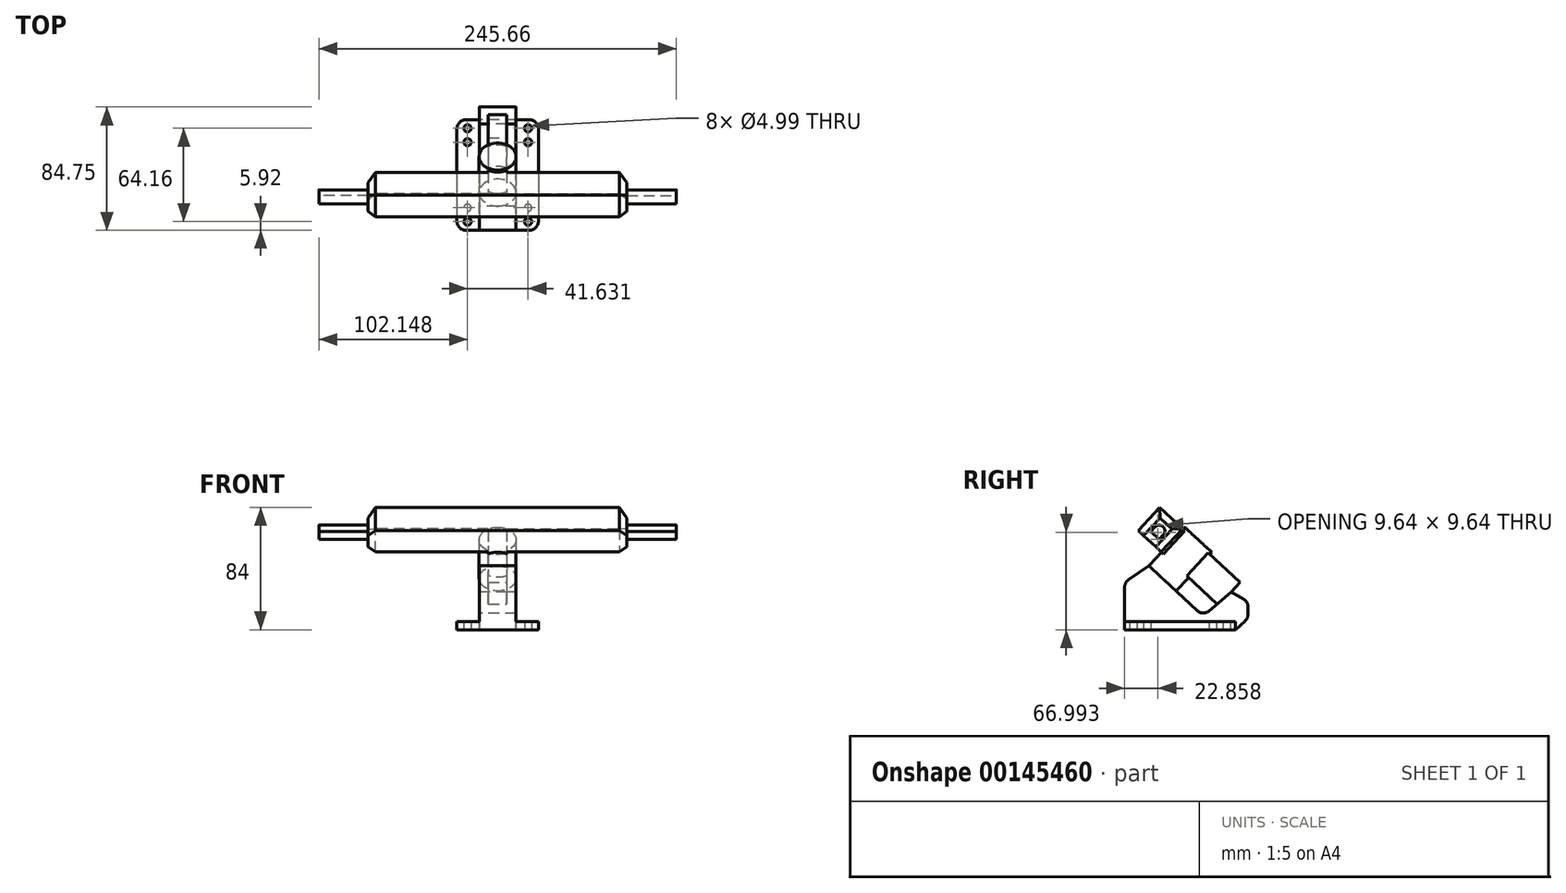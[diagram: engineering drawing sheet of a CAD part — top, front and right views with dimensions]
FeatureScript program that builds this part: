
annotation { "Feature Type Name" : "Feature", "Feature Type Description" : "" }
export const myFeature = defineFeature(function(context is Context, id is Id, definition is map)
    precondition{}
    {
        {
            var Q0;
            Q0=qCreatedBy(makeId("Top.planeOp"),FACE);
            var sketch = newSketch(context, id + "F0", { "sketchPlane" : qUnion([Q0])});
            skLineSegment(sketch, "E0.bottom", {"start": v(-21.65, 38) * mm, "end": v(21.65, 38) * mm});
            skLineSegment(sketch, "E0.top", {"start": v(-21.65, -38) * mm, "end": v(21.65, -38) * mm});
            skLineSegment(sketch, "E0.left", {"start": v(-28, 31.65) * mm, "end": v(-28, -31.65) * mm});
            skLineSegment(sketch, "E0.right", {"start": v(28, 31.65) * mm, "end": v(28, -31.65) * mm});
            skPoint(sketch, "E0.middle", {"position": v(0, 0) * mm});
            skLineSegment(sketch, "E1", {"start": v(20.95, 38) * mm, "end": v(20.95, -38) * mm, "construction": true});
            skLineSegment(sketch, "E2", {"start": v(-20.68, 38) * mm, "end": v(-20.68, -38) * mm, "construction": true});
            skLineSegment(sketch, "E3", {"start": v(-28, 32.08) * mm, "end": v(28, 32.08) * mm, "construction": true});
            skLineSegment(sketch, "E4", {"start": v(-28, 22.52) * mm, "end": v(28, 22.52) * mm, "construction": true});
            skLineSegment(sketch, "E5", {"start": v(-28, -22.52) * mm, "end": v(28, -22.52) * mm, "construction": true});
            skLineSegment(sketch, "E6", {"start": v(28, -32.08) * mm, "end": v(-28, -32.08) * mm, "construction": true});
            skCircle(sketch, "E7", {"center": v(-20.68, -32.08) * mm, "radius": 2.5 * mm});
            skCircle(sketch, "E8", {"center": v(-20.68, -22.52) * mm, "radius": 2.5 * mm});
            skCircle(sketch, "E9", {"center": v(-20.68, 22.52) * mm, "radius": 2.5 * mm});
            skCircle(sketch, "E10", {"center": v(-20.68, 32.08) * mm, "radius": 2.5 * mm});
            skCircle(sketch, "E11", {"center": v(20.95, 32.08) * mm, "radius": 2.5 * mm});
            skCircle(sketch, "E12", {"center": v(20.95, 22.52) * mm, "radius": 2.5 * mm});
            skCircle(sketch, "E13", {"center": v(20.95, -22.52) * mm, "radius": 2.5 * mm});
            skCircle(sketch, "E14", {"center": v(20.95, -32.08) * mm, "radius": 2.5 * mm});
            skPoint(sketch, "E15.visualSharp", {"position": v(-28, 38) * mm});
            skArc(sketch, "E15.filletArc", {"start": v(-21.65, 38) * mm, "mid": v(-26.14, 36.14) * mm, "end": v(-28, 31.65) * mm});
            skPoint(sketch, "E16.visualSharp", {"position": v(-28, -38) * mm});
            skArc(sketch, "E16.filletArc", {"start": v(-28, -31.65) * mm, "mid": v(-26.14, -36.14) * mm, "end": v(-21.65, -38) * mm});
            skPoint(sketch, "E17.visualSharp", {"position": v(28, -38) * mm});
            skArc(sketch, "E17.filletArc", {"start": v(21.65, -38) * mm, "mid": v(26.14, -36.14) * mm, "end": v(28, -31.65) * mm});
            skPoint(sketch, "E18.visualSharp", {"position": v(28, 38) * mm});
            skArc(sketch, "E18.filletArc", {"start": v(28, 31.65) * mm, "mid": v(26.14, 36.14) * mm, "end": v(21.65, 38) * mm});
            skSolve(sketch);
        }
        {
            var Q0;
            Q0 = qSketchRegion(id + "F0", true);
            extrude(context, id + "F1", {"entities" : qUnion([Q0]), "depth" : 5.5 * mm});
        }
        {
            var Q0;
            Q0=qCreatedBy(makeId("Right.planeOp"),FACE);
            var sketch = newSketch(context, id + "F2", { "sketchPlane" : qUnion([Q0])});
            skLineSegment(sketch, "E19", {"start": v(38, 0) * mm, "end": v(44.67, 6.05) * mm});
            skLineSegment(sketch, "E20", {"start": v(46.75, 10.75) * mm, "end": v(46.75, 15.62) * mm});
            skLineSegment(sketch, "E21", {"start": v(43.47, 21.18) * mm, "end": v(35.08, 25.82) * mm});
            skLineSegment(sketch, "E22", {"start": v(35.08, 25.82) * mm, "end": v(20.1, 13) * mm});
            skLineSegment(sketch, "E23", {"start": v(11.63, 13.18) * mm, "end": v(-21.35, 43.97) * mm});
            skLineSegment(sketch, "E24", {"start": v(-21.35, 43.97) * mm, "end": v(-35.25, 34.44) * mm});
            skLineSegment(sketch, "E25", {"start": v(-38, 0) * mm, "end": v(-38, 29.2) * mm});
            skLineSegment(sketch, "E26", {"start": v(-38, 0) * mm, "end": v(38, 0) * mm});
            skPoint(sketch, "E27.visualSharp", {"position": v(15.78, 9.3) * mm});
            skArc(sketch, "E27.filletArc", {"start": v(11.63, 13.18) * mm, "mid": v(15.83, 11.48) * mm, "end": v(20.1, 13) * mm});
            skPoint(sketch, "E28.visualSharp", {"position": v(-38, 32.55) * mm});
            skArc(sketch, "E28.filletArc", {"start": v(-35.25, 34.44) * mm, "mid": v(-37.27, 32.16) * mm, "end": v(-38, 29.2) * mm});
            skPoint(sketch, "E29.visualSharp", {"position": v(46.75, 19.37) * mm});
            skArc(sketch, "E29.filletArc", {"start": v(46.75, 15.62) * mm, "mid": v(45.87, 18.85) * mm, "end": v(43.47, 21.18) * mm});
            skPoint(sketch, "E30.visualSharp", {"position": v(46.75, 7.94) * mm});
            skArc(sketch, "E30.filletArc", {"start": v(44.67, 6.05) * mm, "mid": v(46.2, 8.18) * mm, "end": v(46.75, 10.75) * mm});
            skSolve(sketch);
        }
        {
            var Q0;
            Q0 = qSketchRegion(id + "F2", true);
            extrude(context, id + "F3", {"entities" : qUnion([Q0]), "operationType" : NewBodyOperationType.ADD, "endBound" : BoundingType.SYMMETRIC, "depth" : 25.27 * mm});
        }
        {
            var Q0;
            Q0=makeQuery(id+"F3.opExtrude","SWEPT_FACE",FACE,{"disambiguationData":[OSD([sQuery(id+"F2.wireOp",EDGE,"E23")])]});
            var sketch = newSketch(context, id + "F4", { "sketchPlane" : qUnion([Q0])});
            skLineSegment(sketch, "E31", {"start": v(0, -45.62) * mm, "end": v(0, 0) * mm, "construction": true});
            skCircle(sketch, "E32", {"center": v(0, -32.92) * mm, "radius": 12.7 * mm});
            skSolve(sketch);
        }
        {
            var Q0;
            Q0 = qSketchRegion(id + "F4", true);
            extrude(context, id + "F5", {"entities" : qUnion([Q0]), "operationType" : NewBodyOperationType.ADD, "depth" : 36.2 * mm});
        }
        {
            var Q0;
            {var subQ0=sQuery(id+"F4.wireOp",EDGE,"E32");var subQ1=sQuery(id+"F2.wireOp",EDGE,"E27.filletArc");var subQ2=sQuery(id+"F2.wireOp",EDGE,"E30.filletArc");var subQ3=sQuery(id+"F2.wireOp",EDGE,"E29.filletArc");var subQ4=sQuery(id+"F2.wireOp",EDGE,"E28.filletArc");var subQ5=sQuery(id+"F2.wireOp",EDGE,"E26");var subQ6=sQuery(id+"F2.wireOp",EDGE,"E25");var subQ7=sQuery(id+"F2.wireOp",EDGE,"E24");var subQ8=sQuery(id+"F2.wireOp",EDGE,"E23");var subQ9=sQuery(id+"F2.wireOp",EDGE,"E22");var subQ10=sQuery(id+"F2.wireOp",EDGE,"E21");var subQ11=sQuery(id+"F2.wireOp",EDGE,"E20");var subQ12=sQuery(id+"F2.wireOp",EDGE,"E19");Q0=makeQuery(id+"F5.boolean.opBoolean","SPLIT",FACE,{"disambiguationData":[TD([makeQuery(id+"F3.opExtrude","CAP_FACE",FACE,{"disambiguationData":[OSD([subQ12,subQ11,subQ10,subQ9,subQ8,subQ7,subQ6,subQ5,subQ1,subQ4,subQ3,subQ2])],"isStart":true}),makeQuery(id+"F3.opExtrude","CAP_FACE",FACE,{"disambiguationData":[OSD([subQ12,subQ11,subQ10,subQ9,subQ8,subQ7,subQ6,subQ5,subQ1,subQ4,subQ3,subQ2])],"isStart":false}),makeQuery(id+"F3.opExtrude","SWEPT_FACE",FACE,{"disambiguationData":[OSD([subQ1])]}),makeQuery(id+"F5.opExtrude","SWEPT_FACE",FACE,{"disambiguationData":[OSD([subQ0])]}),makeQuery(id+"F5.opExtrude","CAP_FACE",FACE,{"disambiguationData":[OSD([subQ0])],"isStart":true})])],"derivedFrom":makeQuery(id+"F3.opExtrude","SWEPT_FACE",FACE,{"disambiguationData":[OSD([subQ8])]})});}
            cPlane(context, id + "F6", {"entities" : qUnion([Q0]), "cplaneType" : CPlaneType.OFFSET, "offset" : 12.7 * mm, "width" : 152.4 * mm, "height" : 152.4 * mm});
        }
        {
            var Q0;
            Q0=qCreatedBy(id+"F6.planeOp",FACE);
            var sketch = newSketch(context, id + "F7", { "sketchPlane" : qUnion([Q0])});
            skLineSegment(sketch, "E33", {"start": v(6.35, 8.02) * mm, "end": v(6.35, 5.72) * mm});
            skLineSegment(sketch, "E34", {"start": v(57.15, -45.95) * mm, "end": v(88.9, -45.95) * mm});
            skLineSegment(sketch, "E35", {"start": v(88.9, -45.95) * mm, "end": v(88.9, -52.78) * mm});
            skLineSegment(sketch, "E36", {"start": v(88.9, -52.78) * mm, "end": v(122.83, -52.78) * mm});
            skLineSegment(sketch, "E37", {"start": v(122.83, -52.78) * mm, "end": v(122.83, -60.71) * mm});
            skLineSegment(sketch, "E38", {"start": v(122.83, -60.71) * mm, "end": v(88.9, -60.71) * mm});
            skLineSegment(sketch, "E39", {"start": v(88.9, -60.71) * mm, "end": v(88.9, -67.54) * mm});
            skLineSegment(sketch, "E40", {"start": v(88.9, -67.54) * mm, "end": v(0, -67.54) * mm});
            skPoint(sketch, "E41.visualSharp", {"position": v(6.35, -45.95) * mm});
            skLineSegment(sketch, "E42.MirrorCS", {"start": v(-88.9, -45.95) * mm, "end": v(-88.9, -52.78) * mm});
            skLineSegment(sketch, "E43.MirrorCS", {"start": v(-6.35, 8.02) * mm, "end": v(-6.35, 5.72) * mm});
            skLineSegment(sketch, "E44.MirrorCS", {"start": v(-122.83, -52.78) * mm, "end": v(-122.83, -60.71) * mm});
            skLineSegment(sketch, "E45.MirrorCS", {"start": v(-88.9, -60.71) * mm, "end": v(-88.9, -67.54) * mm});
            skLineSegment(sketch, "E46.MirrorCS", {"start": v(-88.9, -52.78) * mm, "end": v(-122.83, -52.78) * mm});
            skLineSegment(sketch, "E47.MirrorCS", {"start": v(-57.15, -45.95) * mm, "end": v(-88.9, -45.95) * mm});
            skLineSegment(sketch, "E48.MirrorCS", {"start": v(-122.83, -60.71) * mm, "end": v(-88.9, -60.71) * mm});
            skPoint(sketch, "E49.MirrorP", {"position": v(-6.35, -45.95) * mm});
            skLineSegment(sketch, "E50.MirrorCS", {"start": v(-88.9, -67.54) * mm, "end": v(0, -67.54) * mm});
            skLineSegment(sketch, "E51", {"start": v(-6.35, 8.02) * mm, "end": v(6.35, 8.02) * mm});
            skLineSegment(sketch, "E52", {"start": v(88.9, -60.71) * mm, "end": v(88.9, -52.78) * mm});
            skLineSegment(sketch, "E53", {"start": v(-88.9, -60.71) * mm, "end": v(-88.9, -52.78) * mm});
            skLineSegment(sketch, "E54", {"start": v(6.35, -45.95) * mm, "end": v(6.35, 5.72) * mm});
            skLineSegment(sketch, "E55", {"start": v(6.35, -45.95) * mm, "end": v(57.15, -45.95) * mm});
            skLineSegment(sketch, "E56", {"start": v(-6.35, 5.72) * mm, "end": v(-6.35, -45.95) * mm});
            skLineSegment(sketch, "E57", {"start": v(-6.35, -45.95) * mm, "end": v(-57.15, -45.95) * mm});
            skSolve(sketch);
        }
        {
            var Q0;
            Q0=makeQuery(id+"F7.imprint","IMPRINT",FACE,{"disambiguationData":[TD([[makeQuery(id+"F7.imprint","IMPRINT",EDGE,{"derivedFrom":sQuery(id+"F7.wireOp",EDGE,"E33")}),-1.0]])]});
            extrude(context, id + "F8", {"entities" : qUnion([Q0]), "operationType" : NewBodyOperationType.ADD, "depth" : 21.59 * mm});
        }
        {
            var Q0;
            Q0=makeQuery(id+"F7.imprint","IMPRINT",FACE,{"disambiguationData":[TD([[makeQuery(id+"F7.imprint","IMPRINT",EDGE,{"derivedFrom":sQuery(id+"F7.wireOp",EDGE,"E36")}),-1.0]])]});
            var Q1;
            Q1=makeQuery(id+"F7.imprint","IMPRINT",FACE,{"disambiguationData":[TD([[makeQuery(id+"F7.imprint","IMPRINT",EDGE,{"derivedFrom":sQuery(id+"F7.wireOp",EDGE,"E44.MirrorCS")}),1.0]])]});
            extrude(context, id + "F9", {"entities" : qUnion([Q0, Q1]), "operationType" : NewBodyOperationType.ADD, "depth" : 13.45 * mm});
        }
        {
            var Q0;
            Q0=makeQuery(id+"F7.imprint","IMPRINT",FACE,{"disambiguationData":[TD([[makeQuery(id+"F7.imprint","IMPRINT",EDGE,{"derivedFrom":sQuery(id+"F7.wireOp",EDGE,"E36")}),-1.0]])]});
            var Q1;
            Q1=makeQuery(id+"F7.imprint","IMPRINT",FACE,{"disambiguationData":[TD([[makeQuery(id+"F7.imprint","IMPRINT",EDGE,{"derivedFrom":sQuery(id+"F7.wireOp",EDGE,"E44.MirrorCS")}),1.0]])]});
            extrude(context, id + "F10", {"entities" : qUnion([Q0, Q1]), "operationType" : NewBodyOperationType.REMOVE, "depth" : 5.5 * mm});
        }
        {
            var Q0;
            Q0=makeQuery(id+"F8.opExtrude","SWEPT_EDGE",EDGE,{"disambiguationData":[OSD([sQuery(id+"F7.wireOp",EDGE,"E39"),sQuery(id+"F7.wireOp",EDGE,"E40")])]});
            var Q1;
            Q1=makeQuery(id+"F8.opExtrude","CAP_EDGE",EDGE,{"disambiguationData":[OSD([sQuery(id+"F7.wireOp",EDGE,"E35"),sQuery(id+"F7.wireOp",EDGE,"E39"),sQuery(id+"F7.wireOp",EDGE,"E52")])],"isStart":false});
            var Q2;
            Q2=makeQuery(id+"F8.opExtrude","SWEPT_EDGE",EDGE,{"disambiguationData":[OSD([sQuery(id+"F7.wireOp",EDGE,"E34"),sQuery(id+"F7.wireOp",EDGE,"E35")])]});
            var Q3;
            {var subQ0=sQuery(id+"F7.wireOp",EDGE,"E52");var subQ5=sQuery(id+"F7.wireOp",EDGE,"E39");var subQ6=sQuery(id+"F7.wireOp",EDGE,"E35");var subQ8=sQuery(id+"F7.wireOp",EDGE,"E38");var subQ11=sQuery(id+"F7.wireOp",EDGE,"E34");var subQ13=makeQuery(id+"F8.opExtrude","CAP_EDGE",EDGE,{"disambiguationData":[OSD([subQ6,subQ5,subQ0])],"isStart":true});Q3=makeQuery(id+"F10.boolean.opBoolean","MERGE",EDGE,{"derivedFrom":[makeQuery(id+"F9.boolean.opBoolean","SPLIT",EDGE,{"disambiguationData":[TD([makeQuery(id+"F8.opExtrude","SWEPT_FACE",FACE,{"disambiguationData":[OSD([subQ11])]})])],"derivedFrom":subQ13}),makeQuery(id+"F9.boolean.opBoolean","SPLIT",EDGE,{"disambiguationData":[TD([makeQuery(id+"F9.opExtrude","SWEPT_FACE",FACE,{"disambiguationData":[OSD([subQ8])]})])],"derivedFrom":subQ13}),makeQuery(id+"F10.opExtrude","CAP_EDGE",EDGE,{"disambiguationData":[OSD([subQ0])],"isStart":true})]});}
            var Q4;
            Q4=makeQuery(id+"F8.opExtrude","CAP_EDGE",EDGE,{"disambiguationData":[OSD([sQuery(id+"F7.wireOp",EDGE,"E42.MirrorCS"),sQuery(id+"F7.wireOp",EDGE,"E45.MirrorCS"),sQuery(id+"F7.wireOp",EDGE,"E53")])],"isStart":false});
            var Q5;
            Q5=makeQuery(id+"F8.opExtrude","SWEPT_EDGE",EDGE,{"disambiguationData":[OSD([sQuery(id+"F7.wireOp",EDGE,"E45.MirrorCS"),sQuery(id+"F7.wireOp",EDGE,"E50.MirrorCS")])]});
            var Q6;
            Q6=makeQuery(id+"F8.opExtrude","SWEPT_EDGE",EDGE,{"disambiguationData":[OSD([sQuery(id+"F7.wireOp",EDGE,"E42.MirrorCS"),sQuery(id+"F7.wireOp",EDGE,"E47.MirrorCS")])]});
            var Q7;
            {var subQ0=sQuery(id+"F7.wireOp",EDGE,"E53");var subQ1=sQuery(id+"F7.wireOp",EDGE,"E45.MirrorCS");var subQ2=sQuery(id+"F7.wireOp",EDGE,"E42.MirrorCS");var subQ6=sQuery(id+"F7.wireOp",EDGE,"E48.MirrorCS");var subQ11=sQuery(id+"F7.wireOp",EDGE,"E47.MirrorCS");var subQ13=makeQuery(id+"F8.opExtrude","CAP_EDGE",EDGE,{"disambiguationData":[OSD([subQ2,subQ1,subQ0])],"isStart":true});Q7=makeQuery(id+"F10.boolean.opBoolean","MERGE",EDGE,{"derivedFrom":[makeQuery(id+"F9.boolean.opBoolean","SPLIT",EDGE,{"disambiguationData":[TD([makeQuery(id+"F8.opExtrude","SWEPT_FACE",FACE,{"disambiguationData":[OSD([subQ11])]})])],"derivedFrom":subQ13}),makeQuery(id+"F9.boolean.opBoolean","SPLIT",EDGE,{"disambiguationData":[TD([makeQuery(id+"F9.opExtrude","SWEPT_FACE",FACE,{"disambiguationData":[OSD([subQ6])]})])],"derivedFrom":subQ13}),makeQuery(id+"F10.opExtrude","CAP_EDGE",EDGE,{"disambiguationData":[OSD([subQ0])],"isStart":true})]});}
            chamfer(context, id + "F11", {"entities" : qUnion([Q0, Q1, Q2, Q3, Q4, Q5, Q6, Q7]), "width" : 5.08 * mm, "tangentPropagation" : true});
        }
        {
            var Q0;
            Q0=makeQuery(id+"F9.opExtrude","CAP_EDGE",EDGE,{"disambiguationData":[OSD([sQuery(id+"F7.wireOp",EDGE,"E38")])],"isStart":false});
            var Q1;
            Q1=makeQuery(id+"F10.boolean.opBoolean","COPY",EDGE,{"derivedFrom":makeQuery(id+"F10.opExtrude","CAP_EDGE",EDGE,{"disambiguationData":[OSD([sQuery(id+"F7.wireOp",EDGE,"E38")])],"isStart":false})});
            var Q2;
            Q2=makeQuery(id+"F10.boolean.opBoolean","COPY",EDGE,{"derivedFrom":makeQuery(id+"F10.opExtrude","CAP_EDGE",EDGE,{"disambiguationData":[OSD([sQuery(id+"F7.wireOp",EDGE,"E36")])],"isStart":false})});
            var Q3;
            Q3=makeQuery(id+"F9.opExtrude","CAP_EDGE",EDGE,{"disambiguationData":[OSD([sQuery(id+"F7.wireOp",EDGE,"E36")])],"isStart":false});
            var Q4;
            Q4=makeQuery(id+"F10.boolean.opBoolean","COPY",EDGE,{"derivedFrom":makeQuery(id+"F10.opExtrude","CAP_EDGE",EDGE,{"disambiguationData":[OSD([sQuery(id+"F7.wireOp",EDGE,"E48.MirrorCS")])],"isStart":false})});
            var Q5;
            Q5=makeQuery(id+"F9.opExtrude","CAP_EDGE",EDGE,{"disambiguationData":[OSD([sQuery(id+"F7.wireOp",EDGE,"E48.MirrorCS")])],"isStart":false});
            var Q6;
            Q6=makeQuery(id+"F9.opExtrude","CAP_EDGE",EDGE,{"disambiguationData":[OSD([sQuery(id+"F7.wireOp",EDGE,"E46.MirrorCS")])],"isStart":false});
            var Q7;
            Q7=makeQuery(id+"F10.boolean.opBoolean","COPY",EDGE,{"derivedFrom":makeQuery(id+"F10.opExtrude","CAP_EDGE",EDGE,{"disambiguationData":[OSD([sQuery(id+"F7.wireOp",EDGE,"E46.MirrorCS")])],"isStart":false})});
            fillet(context, id + "F12", {"entities" : qUnion([Q0, Q1, Q2, Q3, Q4, Q5, Q6, Q7]), "radius" : 3.8 * mm, "tangentPropagation" : true, "allowEdgeOverflow" : false});
        }
    });
